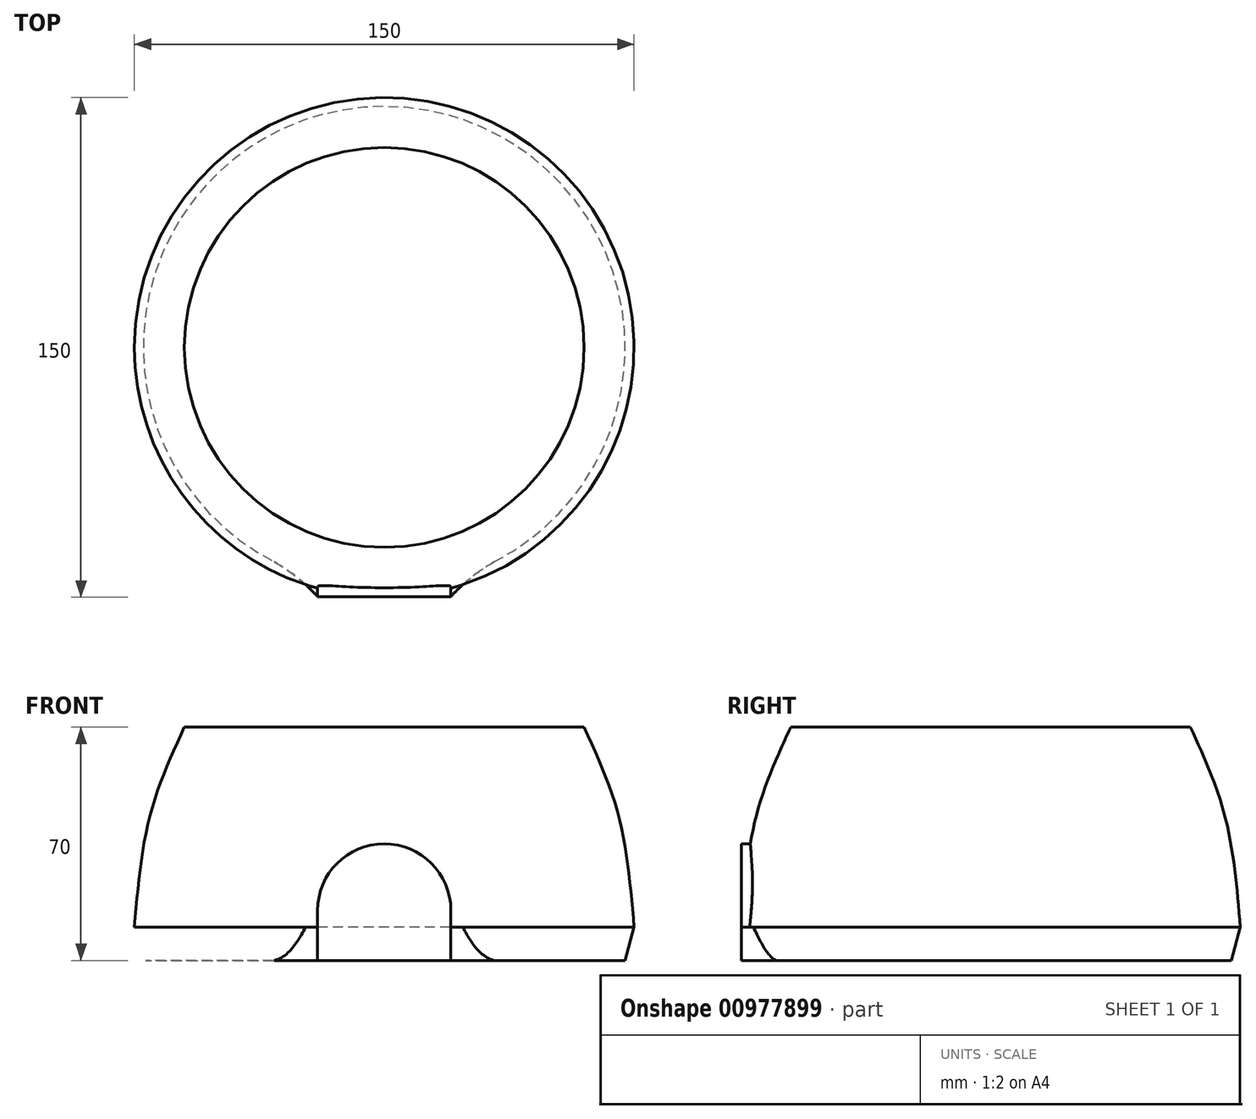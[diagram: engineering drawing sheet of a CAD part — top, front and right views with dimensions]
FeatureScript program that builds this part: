
annotation { "Feature Type Name" : "Feature", "Feature Type Description" : "" }
export const myFeature = defineFeature(function(context is Context, id is Id, definition is map)
    precondition{}
    {
        {
            var Q0;
            Q0=qCreatedBy(makeId("Top.planeOp"),FACE);
            var sketch = newSketch(context, id + "F0", { "sketchPlane" : qUnion([Q0])});
            skArc(sketch, "E0", {"start": v(20, -72.28) * mm, "mid": v(0, 75) * mm, "end": v(-20, -72.28) * mm});
            skCircle(sketch, "E1", {"center": v(0, 0) * mm, "radius": 70 * mm});
            skLineSegment(sketch, "E2", {"start": v(0, -70) * mm, "end": v(-20, -70) * mm});
            skLineSegment(sketch, "E3", {"start": v(0, -70) * mm, "end": v(20, -70) * mm});
            skLineSegment(sketch, "E4", {"start": v(20, -70) * mm, "end": v(20, -72.28) * mm});
            skLineSegment(sketch, "E5", {"start": v(20, -72.28) * mm, "end": v(-20, -72.28) * mm});
            skLineSegment(sketch, "E6", {"start": v(-20, -72.28) * mm, "end": v(-20, -70) * mm});
            skSolve(sketch);
        }
        {
            var Q0;
            Q0=qCreatedBy(makeId("Front.planeOp"),FACE);
            var sketch = newSketch(context, id + "F1", { "sketchPlane" : qUnion([Q0])});
            skLineSegment(sketch, "E7", {"start": v(0, 0) * mm, "end": v(0, 60) * mm});
            skLineSegment(sketch, "E8", {"start": v(0, 60) * mm, "end": v(-60, 60) * mm});
            skLineSegment(sketch, "E9", {"start": v(0, 0) * mm, "end": v(-75, 0) * mm});
            skFitSpline(sketch, "E10", {"points": [v(-75, 0) * mm, v(-70.35, 33.31) * mm, v(-60, 60) * mm], "startDerivative": vector(5.65, 66.23) * mm, "endDerivative": vector(24.6, 53.6) * mm});
            skSolve(sketch);
        }
        {
            var Q0;
            Q0=makeQuery(id+"F1.imprint","IMPRINT",FACE,{"disambiguationData":[TD([[makeQuery(id+"F1.imprint","IMPRINT",EDGE,{"derivedFrom":sQuery(id+"F1.wireOp",EDGE,"E7")}),1.0]])]});
            var Q1;
            Q1=sQuery(id+"F1.wireOp",EDGE,"E7");
            revolve(context, id + "F2", {"surfaceOperationType" : NewSurfaceOperationType.NEW, "entities" : qUnion([Q0]), "axis" : qUnion([Q1]), "revolveType" : RevolveType.FULL});
        }
        {
            var Q0;
            Q0=makeQuery(id+"F0.imprint","IMPRINT",FACE,{"disambiguationData":[TD([[makeQuery(id+"F0.imprint","IMPRINT",EDGE,{"derivedFrom":sQuery(id+"F0.wireOp",EDGE,"E0")}),1.0]])]});
            var Q1;
            Q1=makeQuery(id+"F0.imprint","IMPRINT",FACE,{"disambiguationData":[TD([[makeQuery(id+"F0.imprint","IMPRINT",EDGE,{"derivedFrom":sQuery(id+"F0.wireOp",EDGE,"E2")}),1.0]])]});
            var Q2;
            Q2=makeQuery(id+"F0.imprint","IMPRINT",FACE,{"disambiguationData":[TD([[makeQuery(id+"F0.imprint","IMPRINT",EDGE,{"derivedFrom":sQuery(id+"F0.wireOp",EDGE,"E1")}),1.0]])]});
            var Q3;
            Q3=sQuery(id+"F0.wireOp",EDGE,"E5");
            var Q4;
            Q4=sQuery(id+"F0.wireOp",EDGE,"E0");
            extrude(context, id + "F3", {"entities" : qUnion([Q0, Q1, Q2]), "operationType" : NewBodyOperationType.ADD, "surfaceEntities" : qUnion([Q3, Q4]), "oppositeDirection" : true, "depth" : 10 * mm, "offsetDistance" : 25 * mm, "hasDraft" : true, "draftAngle" : 15 * degree, "draftPullDirection" : true});
        }
        {
            var Q0;
            Q0=makeQuery(id+"F2.opRevolve","SWEPT_FACE",FACE,{"disambiguationData":[OSD([sQuery(id+"F1.wireOp",EDGE,"E9")])]});
            var sketch = newSketch(context, id + "F4", { "sketchPlane" : qUnion([Q0])});
            skLineSegment(sketch, "E11.bottom", {"start": v(-20, 72.28) * mm, "end": v(20, 72.28) * mm});
            skLineSegment(sketch, "E11.top", {"start": v(-20, 81.37) * mm, "end": v(20, 81.37) * mm});
            skLineSegment(sketch, "E11.left", {"start": v(-20, 72.28) * mm, "end": v(-20, 81.37) * mm});
            skLineSegment(sketch, "E11.right", {"start": v(20, 72.28) * mm, "end": v(20, 81.37) * mm});
            skSolve(sketch);
        }
        {
            var Q0;
            Q0 = qSketchRegion(id + "F4", true);
            extrude(context, id + "F5", {"entities" : qUnion([Q0]), "operationType" : NewBodyOperationType.REMOVE, "endBound" : BoundingType.THROUGH_ALL, "oppositeDirection" : true, "depth" : 25 * mm, "offsetDistance" : 25 * mm});
        }
        {
            var Q0;
            Q0=makeQuery(id+"F5.boolean.opBoolean","COPY",FACE,{"derivedFrom":makeQuery(id+"F5.opExtrude","SWEPT_FACE",FACE,{"disambiguationData":[OSD([sQuery(id+"F4.wireOp",EDGE,"E11.bottom")])]})});
            extrude(context, id + "F6", {"entities" : qUnion([Q0]), "operationType" : NewBodyOperationType.ADD, "depth" : 2.5 * mm, "offsetDistance" : 25 * mm});
        }
        {
            var Q0;
            Q0=makeQuery(id+"F6.opExtrude","SWEPT_FACE",FACE,{"disambiguationData":[OSD([sQuery(id+"F0.wireOp",EDGE,"E5"),sQuery(id+"F4.wireOp",EDGE,"E11.bottom")])]});
            var Q1;
            Q1=makeQuery(id+"F3.opExtrude","CAP_FACE",FACE,{"disambiguationData":[OSD([sQuery(id+"F0.wireOp",EDGE,"E0"),sQuery(id+"F0.wireOp",EDGE,"E5")])],"isStart":false});
            extrude(context, id + "F7", {"entities" : qUnion([Q0]), "operationType" : NewBodyOperationType.ADD, "endBound" : BoundingType.UP_TO_SURFACE, "depth" : 25 * mm, "endBoundEntityFace" : qUnion([Q1]), "offsetDistance" : 25 * mm});
        }
        {
            var Q0;
            {var subQ0=sQuery(id+"F4.wireOp",EDGE,"E11.bottom");var subQ1=sQuery(id+"F0.wireOp",EDGE,"E5");Q0=makeQuery(id+"F7.opExtrude","SWEPT_FACE",FACE,{"disambiguationData":[OSD([subQ1,subQ0]),TDD([makeQuery(id+"F6.boolean.opBoolean","MERGE",EDGE,{"derivedFrom":[makeQuery(id+"F5.boolean.opBoolean","MERGE",EDGE,{"derivedFrom":[makeQuery(id+"F3.opExtrude","CAP_EDGE",EDGE,{"disambiguationData":[OSD([subQ1])],"isStart":true})],"fromTools":[makeQuery(id+"F5.opExtrude","CAP_EDGE",EDGE,{"disambiguationData":[OSD([subQ0])],"isStart":true})]}),makeQuery(id+"F6.opExtrude","CAP_EDGE",EDGE,{"disambiguationData":[OSD([subQ1,subQ0])],"isStart":true})]})])]});}
            extrude(context, id + "F8", {"entities" : qUnion([Q0]), "operationType" : NewBodyOperationType.ADD, "endBound" : BoundingType.UP_TO_NEXT, "depth" : 25 * mm, "offsetDistance" : 25 * mm});
        }
        {
            var Q0;
            {var subQ0=sQuery(id+"F4.wireOp",EDGE,"E11.bottom");var subQ1=sQuery(id+"F0.wireOp",EDGE,"E5");Q0=makeQuery(id+"F7.boolean.opBoolean","MERGE",FACE,{"derivedFrom":[makeQuery(id+"F6.opExtrude","CAP_FACE",FACE,{"disambiguationData":[OSD([subQ0])],"isStart":false}),makeQuery(id+"F7.opExtrude","SWEPT_FACE",FACE,{"disambiguationData":[OSD([subQ1,subQ0]),TDD([makeQuery(id+"F6.opExtrude","CAP_EDGE",EDGE,{"disambiguationData":[OSD([subQ1,subQ0])],"isStart":false})])]})]});}
            var sketch = newSketch(context, id + "F9", { "sketchPlane" : qUnion([Q0])});
            skLineSegment(sketch, "E12.bottom", {"start": v(-20, -10) * mm, "end": v(20, -10) * mm});
            skLineSegment(sketch, "E12.top", {"start": v(-20, 25) * mm, "end": v(20, 25) * mm});
            skLineSegment(sketch, "E12.left", {"start": v(-20, -10) * mm, "end": v(-20, 25) * mm});
            skLineSegment(sketch, "E12.right", {"start": v(20, -10) * mm, "end": v(20, 25) * mm});
            skSolve(sketch);
        }
        {
            var Q0;
            Q0 = qSketchRegion(id + "F9", true);
            extrude(context, id + "F10", {"entities" : qUnion([Q0]), "operationType" : NewBodyOperationType.ADD, "endBound" : BoundingType.UP_TO_NEXT, "oppositeDirection" : true, "depth" : 25 * mm, "offsetDistance" : 25 * mm});
        }
        {
            var Q0;
            {var subQ0=sQuery(id+"F4.wireOp",EDGE,"E11.bottom");var subQ1=sQuery(id+"F0.wireOp",EDGE,"E5");Q0=makeQuery(id+"F8.boolean.opBoolean","MERGE",FACE,{"derivedFrom":[makeQuery(id+"F3.opExtrude","CAP_FACE",FACE,{"disambiguationData":[OSD([sQuery(id+"F0.wireOp",EDGE,"E0"),subQ1])],"isStart":false}),makeQuery(id+"F7.opExtrude","CAP_FACE",FACE,{"disambiguationData":[OSD([subQ1,subQ0])],"isStart":false}),makeQuery(id+"F8.opExtrude","SWEPT_FACE",FACE,{"disambiguationData":[OSD([subQ1,subQ0])]})]});}
            var sketch = newSketch(context, id + "F11", { "sketchPlane" : qUnion([Q0])});
            skArc(sketch, "E13", {"start": v(20, 74.78) * mm, "mid": v(27.32, 68.13) * mm, "end": v(35.72, 62.89) * mm});
            skArc(sketch, "E14.MirrorCS", {"start": v(-20, 74.78) * mm, "mid": v(-27.32, 68.13) * mm, "end": v(-35.72, 62.89) * mm});
            skSolve(sketch);
        }
        {
            var Q0;
            {var subQ1=sQuery(id+"F4.wireOp",EDGE,"E11.left");var subQ2=sQuery(id+"F4.wireOp",EDGE,"E11.bottom");var subQ3=sQuery(id+"F1.wireOp",EDGE,"E10");var subQ4=sQuery(id+"F1.wireOp",EDGE,"E9");var subQ5=sQuery(id+"F0.wireOp",EDGE,"E6");var subQ6=sQuery(id+"F0.wireOp",EDGE,"E5");var subQ7=sQuery(id+"F0.wireOp",EDGE,"E0");var subQ8=makeQuery(id+"F10.boolean.opBoolean","MERGE",EDGE,{"derivedFrom":[makeQuery(id+"F7.opExtrude","CAP_EDGE",EDGE,{"disambiguationData":[OSD([subQ7,subQ6,subQ5,subQ4,subQ3,subQ2,subQ1])],"isStart":false}),makeQuery(id+"F8.opExtrude","SWEPT_EDGE",EDGE,{"disambiguationData":[OSD([subQ7,subQ6,subQ5,subQ4,subQ3,subQ2,subQ1])]})]});Q0=makeQuery(id+"F11.imprint","IMPRINT",FACE,{"disambiguationData":[TD([[makeQuery(id+"F11.imprint","IMPRINT",EDGE,{"derivedFrom":subQ8}),1.0]])]});}
            var Q1;
            {var subQ1=sQuery(id+"F4.wireOp",EDGE,"E11.right");var subQ2=sQuery(id+"F4.wireOp",EDGE,"E11.bottom");var subQ3=sQuery(id+"F1.wireOp",EDGE,"E10");var subQ4=sQuery(id+"F1.wireOp",EDGE,"E9");var subQ5=sQuery(id+"F0.wireOp",EDGE,"E5");var subQ6=sQuery(id+"F0.wireOp",EDGE,"E4");var subQ7=sQuery(id+"F0.wireOp",EDGE,"E0");var subQ8=makeQuery(id+"F10.boolean.opBoolean","MERGE",EDGE,{"derivedFrom":[makeQuery(id+"F7.opExtrude","CAP_EDGE",EDGE,{"disambiguationData":[OSD([subQ7,subQ6,subQ5,subQ4,subQ3,subQ2,subQ1])],"isStart":false}),makeQuery(id+"F8.opExtrude","SWEPT_EDGE",EDGE,{"disambiguationData":[OSD([subQ7,subQ6,subQ5,subQ4,subQ3,subQ2,subQ1])]})]});Q1=makeQuery(id+"F11.imprint","IMPRINT",FACE,{"disambiguationData":[TD([[makeQuery(id+"F11.imprint","IMPRINT",EDGE,{"derivedFrom":subQ8}),-1.0]])]});}
            extrude(context, id + "F12", {"entities" : qUnion([Q0, Q1]), "operationType" : NewBodyOperationType.ADD, "oppositeDirection" : true, "depth" : 10 * mm, "offsetDistance" : 25 * mm});
        }
        {
            var Q0;
            Q0=makeQuery(id+"F10.opExtrude","SWEPT_EDGE",EDGE,{"disambiguationData":[OSD([sQuery(id+"F9.wireOp",EDGE,"E12.top"),sQuery(id+"F9.wireOp",EDGE,"E12.right")])]});
            var Q1;
            Q1=makeQuery(id+"F10.opExtrude","SWEPT_EDGE",EDGE,{"disambiguationData":[OSD([sQuery(id+"F9.wireOp",EDGE,"E12.top"),sQuery(id+"F9.wireOp",EDGE,"E12.left")])]});
            fillet(context, id + "F13", {"entities" : qUnion([Q0, Q1]), "radius" : 20 * mm, "tangentPropagation" : true, "allowEdgeOverflow" : false});
        }
    });
